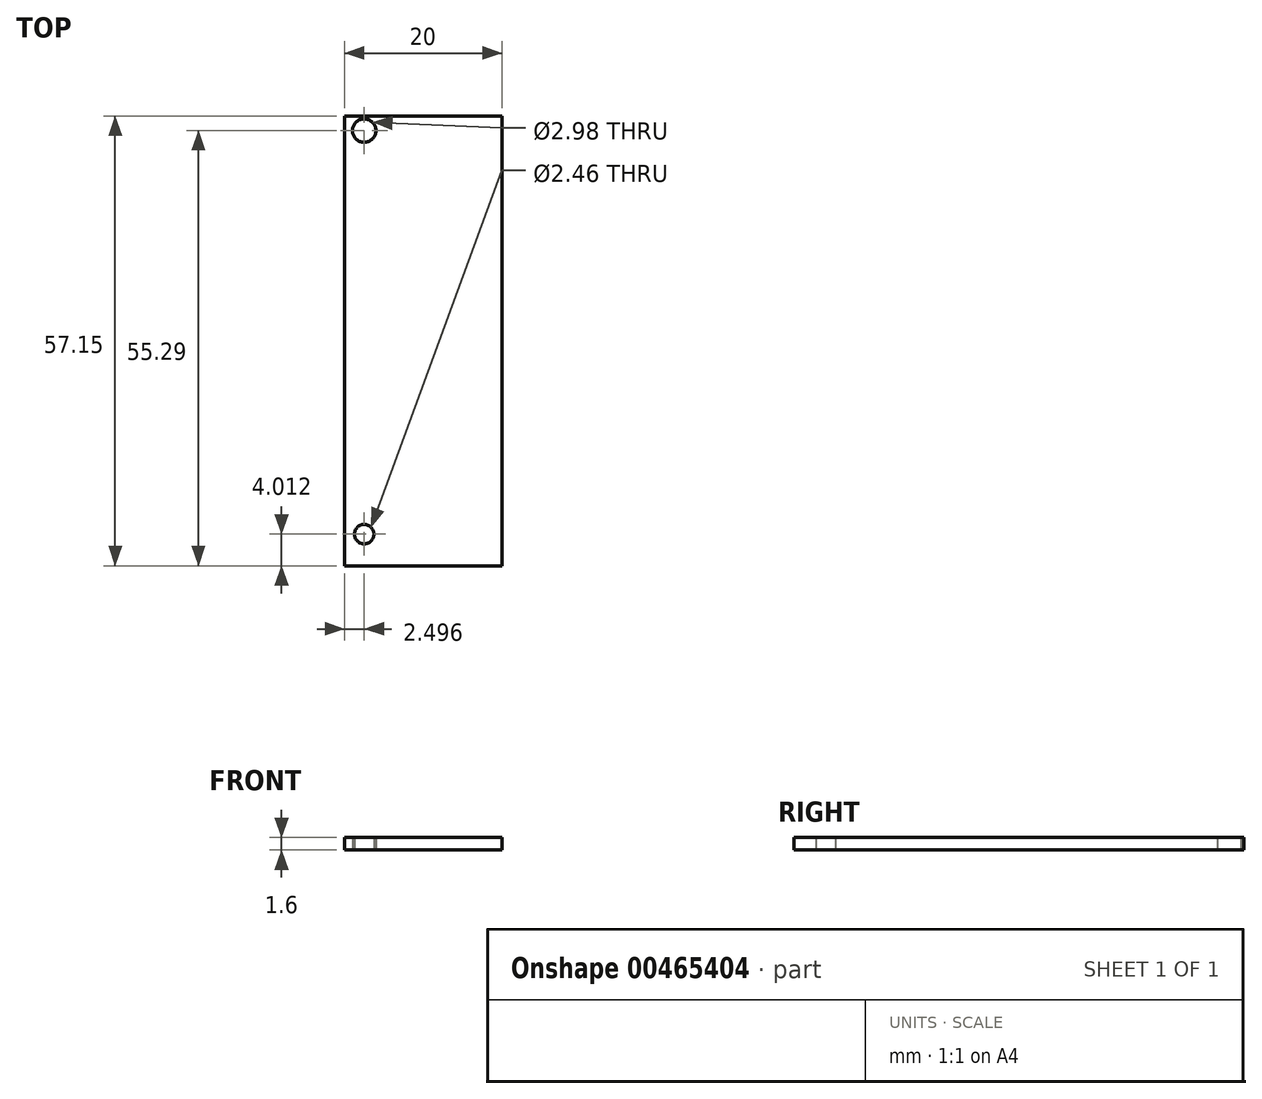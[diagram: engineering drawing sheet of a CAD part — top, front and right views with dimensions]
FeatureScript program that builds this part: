
annotation { "Feature Type Name" : "Feature", "Feature Type Description" : "" }
export const myFeature = defineFeature(function(context is Context, id is Id, definition is map)
    precondition{}
    {
        {
            var Q0;
            Q0=qCreatedBy(makeId("Top.planeOp"),FACE);
            var sketch = newSketch(context, id + "F0", { "sketchPlane" : qUnion([Q0])});
            skLineSegment(sketch, "E0.bottom", {"start": v(0, 0) * mm, "end": v(20, 0) * mm});
            skLineSegment(sketch, "E0.top", {"start": v(0, -57.15) * mm, "end": v(20, -57.15) * mm});
            skLineSegment(sketch, "E0.left", {"start": v(0, 0) * mm, "end": v(0, -57.15) * mm});
            skLineSegment(sketch, "E0.right", {"start": v(20, 0) * mm, "end": v(20, -57.15) * mm});
            skCircle(sketch, "E1", {"center": v(2.5, -1.86) * mm, "radius": 1.49 * mm});
            skCircle(sketch, "E2", {"center": v(2.5, -53.14) * mm, "radius": 1.23 * mm});
            skSolve(sketch);
        }
        {
            var Q0;
            Q0=makeQuery(id+"F0.imprint","IMPRINT",FACE,{"disambiguationData":[TD([[makeQuery(id+"F0.imprint","IMPRINT",EDGE,{"derivedFrom":sQuery(id+"F0.wireOp",EDGE,"E0.bottom")}),-1.0]])]});
            extrude(context, id + "F1", {"entities" : qUnion([Q0]), "depth" : 1.6 * mm, "offsetDistance" : 25 * mm});
        }
    });
